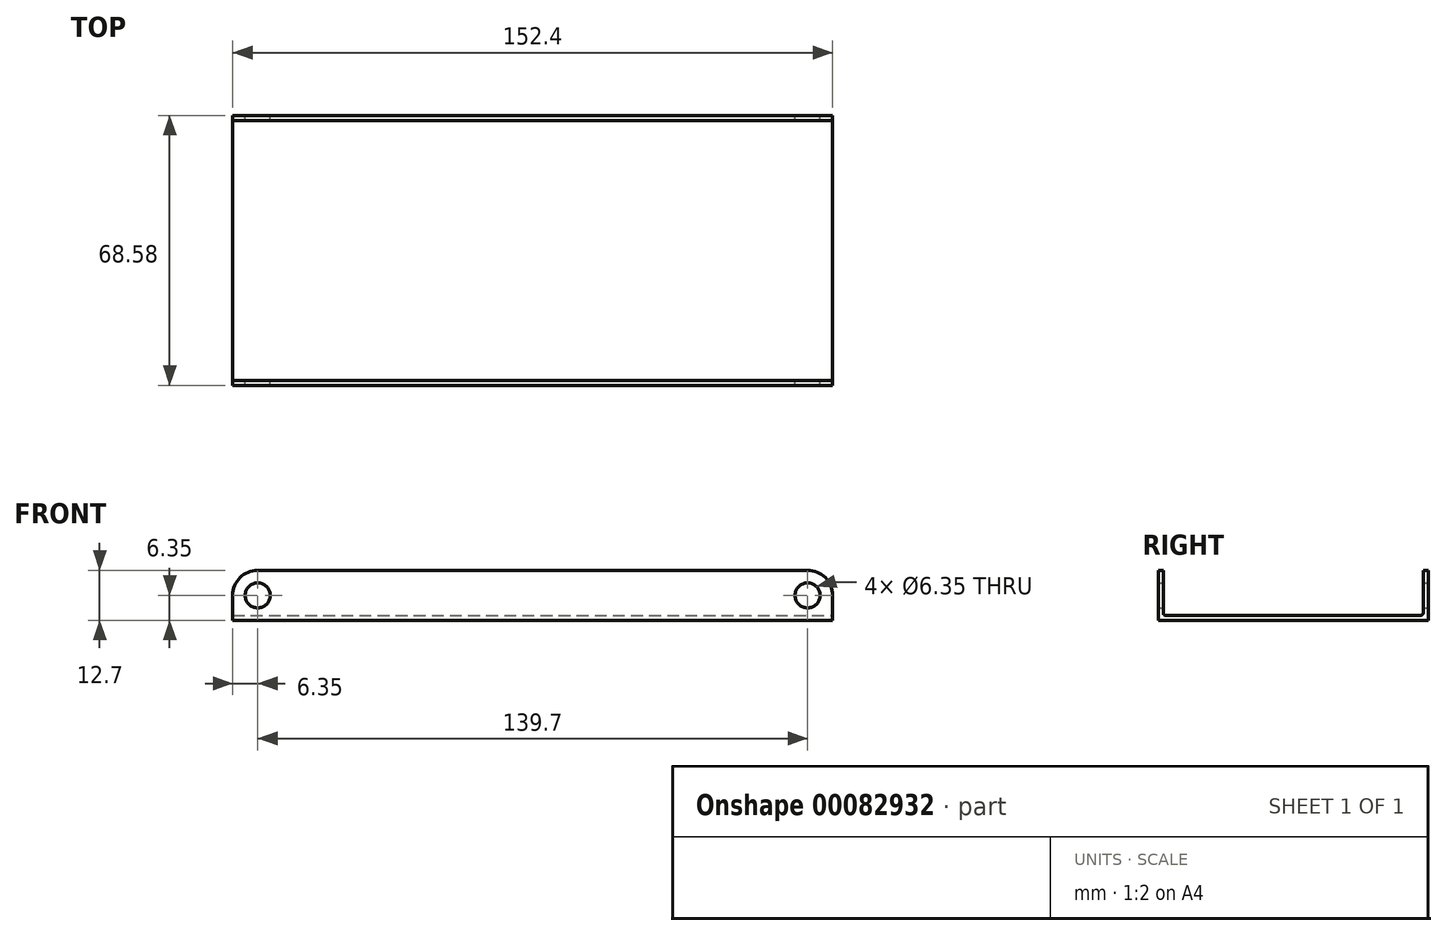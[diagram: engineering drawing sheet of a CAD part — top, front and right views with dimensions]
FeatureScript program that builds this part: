
annotation { "Feature Type Name" : "Feature", "Feature Type Description" : "" }
export const myFeature = defineFeature(function(context is Context, id is Id, definition is map)
    precondition{}
    {
        {
            var Q0;
            Q0=qCreatedBy(makeId("Front.planeOp"),FACE);
            var sketch = newSketch(context, id + "F0", { "sketchPlane" : qUnion([Q0])});
            skLineSegment(sketch, "E0.bottom", {"start": v(0, 0) * mm, "end": v(-152.4, 0) * mm});
            skLineSegment(sketch, "E0.top", {"start": v(0, 12.7) * mm, "end": v(-152.4, 12.7) * mm});
            skLineSegment(sketch, "E0.left", {"start": v(0, 0) * mm, "end": v(0, 12.7) * mm});
            skLineSegment(sketch, "E0.right", {"start": v(-152.4, 0) * mm, "end": v(-152.4, 12.7) * mm});
            skCircle(sketch, "E1", {"center": v(-146.05, 6.35) * mm, "radius": 3.18 * mm});
            skLineSegment(sketch, "E2", {"start": v(-146.05, 6.35) * mm, "end": v(-146.05, 12.7) * mm, "construction": true});
            skLineSegment(sketch, "E3", {"start": v(-146.05, 12.7) * mm, "end": v(-146.05, 6.35) * mm, "construction": true});
            skLineSegment(sketch, "E4", {"start": v(-146.05, 6.35) * mm, "end": v(-152.4, 6.35) * mm, "construction": true});
            skArc(sketch, "E5", {"start": v(-146.05, 12.7) * mm, "mid": v(-150.54, 10.84) * mm, "end": v(-152.4, 6.35) * mm});
            skLineSegment(sketch, "E6", {"start": v(-76.2, 12.7) * mm, "end": v(-76.2, 0) * mm, "construction": true});
            skCircle(sketch, "E7.MirrorC", {"center": v(-6.35, 6.35) * mm, "radius": 3.18 * mm});
            skArc(sketch, "E8.MirrorCS", {"start": v(-6.35, 12.7) * mm, "mid": v(-1.86, 10.84) * mm, "end": v(0, 6.35) * mm});
            skSolve(sketch);
        }
        {
            var Q0;
            {var subQ1=sQuery(id+"F0.wireOp",EDGE,"E0.bottom");Q0=makeQuery(id+"F0.imprint","IMPRINT",FACE,{"disambiguationData":[TD([[makeQuery(id+"F0.imprint","IMPRINT",EDGE,{"derivedFrom":subQ1}),-1.0]])]});}
            extrude(context, id + "F1", {"entities" : qUnion([Q0]), "depth" : 68.58 * mm});
        }
        {
            var Q0;
            Q0=makeQuery(id+"F1.opExtrude","SWEPT_FACE",FACE,{"disambiguationData":[OSD([sQuery(id+"F0.wireOp",EDGE,"E0.top")])]});
            var sketch = newSketch(context, id + "F2", { "sketchPlane" : qUnion([Q0])});
            skLineSegment(sketch, "E9.0", {"start": v(-6.35, 0) * mm, "end": v(-146.05, 0) * mm});
            skLineSegment(sketch, "E9.1", {"start": v(-6.35, -68.58) * mm, "end": v(-146.05, -68.58) * mm});
            skLineSegment(sketch, "E10.bottom", {"start": v(-177.91, -1.27) * mm, "end": v(2.46, -1.27) * mm});
            skLineSegment(sketch, "E10.top", {"start": v(-177.91, -67.31) * mm, "end": v(2.46, -67.3) * mm});
            skLineSegment(sketch, "E10.left", {"start": v(-177.91, -1.27) * mm, "end": v(-177.91, -67.31) * mm});
            skLineSegment(sketch, "E10.right", {"start": v(2.46, -1.27) * mm, "end": v(2.46, -67.3) * mm});
            skSolve(sketch);
        }
        {
            var Q0;
            {var subQ0=sQuery(id+"F2.wireOp",EDGE,"E10.bottom");var subQ1=sQuery(id+"F0.wireOp",EDGE,"E0.top");var subQ2=makeQuery(id+"F1.opExtrude","SWEPT_EDGE",EDGE,{"disambiguationData":[OSD([subQ1,sQuery(id+"F0.wireOp",EDGE,"E5")])]});var subQ3=makeQuery(id+"F2.imprint","INTERSECT",VERTEX,{"derivedFrom":[subQ2,subQ0]});Q0=makeQuery(id+"F2.imprint","IMPRINT",FACE,{"disambiguationData":[TD([[makeQuery(id+"F2.imprint","IMPRINT",EDGE,{"disambiguationData":[TD([[subQ3,-1.0]])],"derivedFrom":subQ0}),-1.0]])]});}
            var Q1;
            {var subQ0=sQuery(id+"F2.wireOp",EDGE,"E10.left");Q1=makeQuery(id+"F2.imprint","IMPRINT",FACE,{"disambiguationData":[TD([[makeQuery(id+"F2.imprint","IMPRINT",EDGE,{"derivedFrom":subQ0}),1.0]])]});}
            var Q2;
            {var subQ0=sQuery(id+"F2.wireOp",EDGE,"E10.right");Q2=makeQuery(id+"F2.imprint","IMPRINT",FACE,{"disambiguationData":[TD([[makeQuery(id+"F2.imprint","IMPRINT",EDGE,{"derivedFrom":subQ0}),-1.0]])]});}
            extrude(context, id + "F3", {"entities" : qUnion([Q0, Q1, Q2]), "operationType" : NewBodyOperationType.REMOVE, "oppositeDirection" : true, "depth" : 11.43 * mm});
        }
        {
            var Q0;
            Q0=makeQuery(id+"F3.boolean.opBoolean","COPY",EDGE,{"derivedFrom":makeQuery(id+"F3.opExtrude","CAP_EDGE",EDGE,{"disambiguationData":[OSD([sQuery(id+"F2.wireOp",EDGE,"E10.bottom")])],"isStart":false})});
            var Q1;
            Q1=makeQuery(id+"F3.boolean.opBoolean","COPY",EDGE,{"derivedFrom":makeQuery(id+"F3.opExtrude","CAP_EDGE",EDGE,{"disambiguationData":[OSD([sQuery(id+"F2.wireOp",EDGE,"E10.top")])],"isStart":false})});
            fillet(context, id + "F4", {"entities" : qUnion([Q0, Q1]), "radius" : 0.64 * mm, "tangentPropagation" : true, "allowEdgeOverflow" : false});
        }
    });
